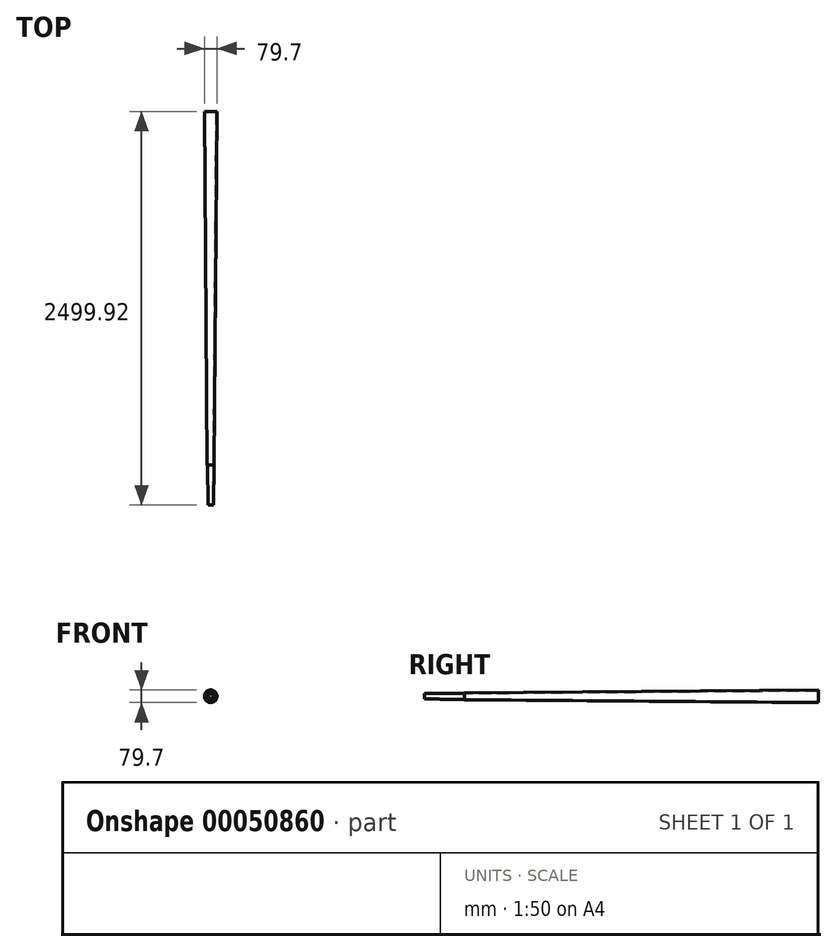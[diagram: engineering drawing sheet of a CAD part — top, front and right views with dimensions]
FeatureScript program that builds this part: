
annotation { "Feature Type Name" : "Feature", "Feature Type Description" : "" }
export const myFeature = defineFeature(function(context is Context, id is Id, definition is map)
    precondition{}
    {
        {
            var Q0;
            Q0=qCreatedBy(makeId("Right.planeOp"),FACE);
            var sketch = newSketch(context, id + "F0", { "sketchPlane" : qUnion([Q0])});
            skLineSegment(sketch, "E0", {"start": v(-2245.95, 22.2) * mm, "end": v(0, 39.85) * mm});
            skLineSegment(sketch, "E1", {"start": v(-2513.36, 0) * mm, "end": v(0, 0) * mm});
            skLineSegment(sketch, "E2", {"start": v(0, 34.77) * mm, "end": v(0, 39.85) * mm});
            skLineSegment(sketch, "E3", {"start": v(-2499.92, 15.13) * mm, "end": v(0, 34.77) * mm});
            skLineSegment(sketch, "E4", {"start": v(-2499.92, 17.67) * mm, "end": v(-2499.92, 15.13) * mm});
            skPoint(sketch, "E5.orphan", {"position": v(-2499.92, 0) * mm});
            skLineSegment(sketch, "E6", {"start": v(-2499.92, 17.67) * mm, "end": v(-2245.93, 19.67) * mm});
            skLineSegment(sketch, "E7", {"start": v(-2245.93, 19.67) * mm, "end": v(-2245.95, 22.2) * mm});
            skPoint(sketch, "E8.orphan", {"position": v(-2499.92, 20.21) * mm});
            skSolve(sketch);
        }
        {
            var Q0;
            Q0=makeQuery(id+"F0.imprint","IMPRINT",FACE,{"disambiguationData":[TD([[makeQuery(id+"F0.imprint","IMPRINT",EDGE,{"derivedFrom":sQuery(id+"F0.wireOp",EDGE,"E0")}),-1.0]])]});
            var Q1;
            Q1=sQuery(id+"F0.wireOp",EDGE,"E3");
            var Q2;
            Q2=sQuery(id+"F0.wireOp",EDGE,"E0");
            var Q3;
            Q3=sQuery(id+"F0.wireOp",EDGE,"E2");
            var Q4;
            Q4=sQuery(id+"F0.wireOp",EDGE,"ddf9b52d-5346-4b2c-8b13-d19e91e52e76");
            var Q5;
            Q5=sQuery(id+"F0.wireOp",EDGE,"E1");
            revolve(context, id + "F1", {"entities" : qUnion([Q0]), "surfaceEntities" : qUnion([Q1, Q2, Q3, Q4]), "axis" : qUnion([Q5]), "revolveType" : RevolveType.FULL});
        }
    });
